# Revit family: Internal block_22_45_CR
name_source: partatom
category: Оборудование
units: mm (PartAtom-declared; Revit-internal decimal feet)

## family parameters
Всегда вертикально = Да
Классификация = Нет
На основе рабочей плоскости = Нет
Общий = Нет
При загрузке вырезать с полостями = Нет
Размер круглого соединителя = Использовать диаметр
Тип детали = Нормальный
Точка принадлежности помещению = Нет

## types (4) — shared parameters
00_20_Manufacturer = BLAUBERG
00_20_Name = Internal block
C = 267 мм
Casing Material = Steel, white, mat
G = 650 мм
Grid Material = Mesh, steel, painted,  white
H = 650 мм
Height = 297 мм
I = 30 мм
I1 = 10 мм
Length = 650 мм
Load Classification = HVAC
Maintenance zone material = <По категории>
Maximum Air Flow = 0.0 л/с
Weight = 17.50 кг
Width = 650 мм
Изготовитель = BLAUBERG
zero-valued in all types: Отметка по умолчанию

## per-type parameters (varying)
| type | Power |
| BLHV-22-I-C4-AC/1R1A | 38 Вт |
| BLHV-28-I-C4-AC/1R1A | 38 Вт |
| BLHV-36-I-C4-AC/1R1A | 40 Вт |
| BLHV-45-I-C4-DC/1R1A | 40 Вт |

note: column(s) folded — value = type name in every type: 00_20_Type
